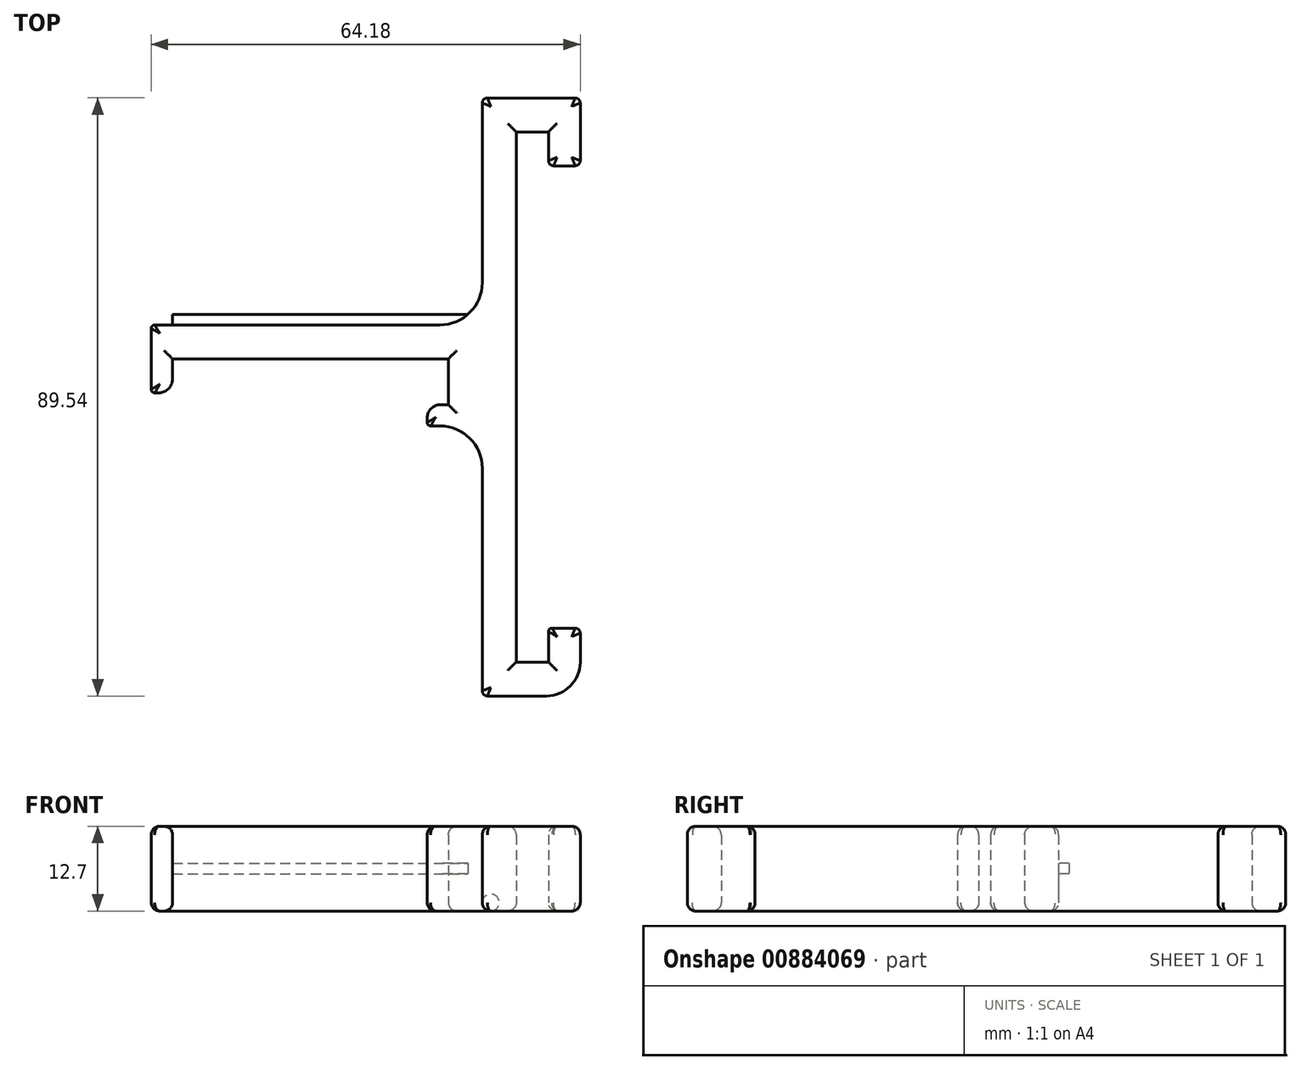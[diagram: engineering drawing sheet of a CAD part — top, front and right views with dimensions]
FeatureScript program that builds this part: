
annotation { "Feature Type Name" : "Feature", "Feature Type Description" : "" }
export const myFeature = defineFeature(function(context is Context, id is Id, definition is map)
    precondition{}
    {
        {
            var Q0;
            Q0=qCreatedBy(makeId("Top.planeOp"),FACE);
            var sketch = newSketch(context, id + "F0", { "sketchPlane" : qUnion([Q0])});
            skLineSegment(sketch, "E0", {"start": v(41.28, 0) * mm, "end": v(0, 0) * mm});
            skLineSegment(sketch, "E1", {"start": v(41.28, -6.86) * mm, "end": v(40.13, -6.86) * mm});
            skLineSegment(sketch, "E2", {"start": v(38.1, -8.89) * mm, "end": v(38.1, -9.53) * mm});
            skLineSegment(sketch, "E3", {"start": v(38.6, -10.03) * mm, "end": v(40, -10.03) * mm});
            skLineSegment(sketch, "E4", {"start": v(0, 0) * mm, "end": v(0, -3.05) * mm});
            skLineSegment(sketch, "E5.0", {"start": v(40, 5.08) * mm, "end": v(-2.67, 5.08) * mm});
            skLineSegment(sketch, "E6.0", {"start": v(-3.18, 4.57) * mm, "end": v(-3.18, -4.57) * mm});
            skLineSegment(sketch, "E7", {"start": v(-2.67, -5.08) * mm, "end": v(-2.03, -5.08) * mm});
            skLineSegment(sketch, "E8.0", {"start": v(55.92, -50.47) * mm, "end": v(47.1, -50.47) * mm});
            skLineSegment(sketch, "E9", {"start": v(46.34, -16.38) * mm, "end": v(46.34, -49.7) * mm});
            skLineSegment(sketch, "E10", {"start": v(46.34, 11.43) * mm, "end": v(46.34, 38.3) * mm});
            skLineSegment(sketch, "E11.0", {"start": v(51.42, 33.99) * mm, "end": v(51.42, -45.39) * mm});
            skLineSegment(sketch, "E12.0", {"start": v(56.25, 33.99) * mm, "end": v(56.25, 29.67) * mm});
            skLineSegment(sketch, "E13.0", {"start": v(56.25, -45.39) * mm, "end": v(51.42, -45.39) * mm});
            skLineSegment(sketch, "E14.0", {"start": v(61, -41.07) * mm, "end": v(61, -45.39) * mm});
            skLineSegment(sketch, "E15.0", {"start": v(56.25, 33.99) * mm, "end": v(51.42, 33.99) * mm});
            skLineSegment(sketch, "E16.0", {"start": v(60.24, 39.07) * mm, "end": v(47.1, 39.07) * mm});
            skLineSegment(sketch, "E17.0", {"start": v(60.24, -40.3) * mm, "end": v(56.76, -40.3) * mm});
            skLineSegment(sketch, "E18", {"start": v(56.25, -40.82) * mm, "end": v(56.25, -45.39) * mm});
            skLineSegment(sketch, "E19.0", {"start": v(60.24, 28.9) * mm, "end": v(57.01, 28.9) * mm});
            skLineSegment(sketch, "E20", {"start": v(61, 38.3) * mm, "end": v(61, 29.67) * mm});
            skLineSegment(sketch, "E21", {"start": v(41.28, 0) * mm, "end": v(41.28, -6.86) * mm});
            skPoint(sketch, "E22.visualSharp", {"position": v(61, -50.47) * mm});
            skArc(sketch, "E22.filletArc", {"start": v(55.92, -50.47) * mm, "mid": v(59.51, -48.98) * mm, "end": v(61, -45.39) * mm});
            skArc(sketch, "E23.filletArc", {"start": v(46.34, -49.7) * mm, "mid": v(46.57, -50.25) * mm, "end": v(47.1, -50.47) * mm});
            skPoint(sketch, "E24.visualSharp", {"position": v(61, -40.3) * mm});
            skArc(sketch, "E24.filletArc", {"start": v(61, -41.07) * mm, "mid": v(60.77, -40.53) * mm, "end": v(60.24, -40.3) * mm});
            skPoint(sketch, "E25.visualSharp", {"position": v(56.25, -40.3) * mm});
            skArc(sketch, "E25.filletArc", {"start": v(56.76, -40.3) * mm, "mid": v(56.4, -40.46) * mm, "end": v(56.25, -40.82) * mm});
            skPoint(sketch, "E26.visualSharp", {"position": v(56.25, 28.9) * mm});
            skArc(sketch, "E26.filletArc", {"start": v(56.25, 29.67) * mm, "mid": v(56.47, 29.13) * mm, "end": v(57.01, 28.9) * mm});
            skPoint(sketch, "E27.visualSharp", {"position": v(61, 28.9) * mm});
            skArc(sketch, "E27.filletArc", {"start": v(60.24, 28.9) * mm, "mid": v(60.77, 29.13) * mm, "end": v(61, 29.67) * mm});
            skPoint(sketch, "E28.visualSharp", {"position": v(61, 39.07) * mm});
            skArc(sketch, "E28.filletArc", {"start": v(61, 38.3) * mm, "mid": v(60.77, 38.84) * mm, "end": v(60.24, 39.07) * mm});
            skPoint(sketch, "E29.visualSharp", {"position": v(46.34, 39.07) * mm});
            skArc(sketch, "E29.filletArc", {"start": v(47.1, 39.07) * mm, "mid": v(46.57, 38.84) * mm, "end": v(46.34, 38.3) * mm});
            skPoint(sketch, "E30.visualSharp", {"position": v(46.34, 5.08) * mm});
            skArc(sketch, "E30.filletArc", {"start": v(40, 5.08) * mm, "mid": v(44.48, 6.94) * mm, "end": v(46.34, 11.43) * mm});
            skPoint(sketch, "E31.visualSharp", {"position": v(46.34, -10.03) * mm});
            skArc(sketch, "E31.filletArc", {"start": v(46.34, -16.38) * mm, "mid": v(44.48, -11.9) * mm, "end": v(40, -10.03) * mm});
            skPoint(sketch, "E32.visualSharp", {"position": v(-3.18, 5.08) * mm});
            skArc(sketch, "E32.filletArc", {"start": v(-2.67, 5.08) * mm, "mid": v(-3.03, 4.93) * mm, "end": v(-3.18, 4.57) * mm});
            skPoint(sketch, "E33.visualSharp", {"position": v(-3.18, -5.08) * mm});
            skArc(sketch, "E33.filletArc", {"start": v(-3.18, -4.57) * mm, "mid": v(-3.03, -4.93) * mm, "end": v(-2.67, -5.08) * mm});
            skPoint(sketch, "E34.visualSharp", {"position": v(38.1, -10.03) * mm});
            skArc(sketch, "E34.filletArc", {"start": v(38.1, -9.53) * mm, "mid": v(38.25, -9.88) * mm, "end": v(38.6, -10.03) * mm});
            skPoint(sketch, "E35.visualSharp", {"position": v(0, -5.08) * mm});
            skArc(sketch, "E35.filletArc", {"start": v(-2.03, -5.08) * mm, "mid": v(-0.6, -4.48) * mm, "end": v(0, -3.05) * mm});
            skPoint(sketch, "E36.visualSharp", {"position": v(38.1, -6.86) * mm});
            skArc(sketch, "E36.filletArc", {"start": v(40.13, -6.86) * mm, "mid": v(38.7, -7.45) * mm, "end": v(38.1, -8.89) * mm});
            skSolve(sketch);
        }
        {
            var Q0;
            Q0=qSketchRegion(id+"F0",true);
            extrude(context, id + "F1", {"entities" : qUnion([Q0]), "depth" : 12.7 * mm, "offsetDistance" : 25.4 * mm});
        }
        {
            var Q0;
            Q0=makeQuery(id+"F1.opExtrude","SWEPT_FACE",FACE,{"disambiguationData":[OSD([sQuery(id+"F0.wireOp",EDGE,"E5.0")])]});
            cPlane(context, id + "F2", {"entities" : qUnion([Q0]), "cplaneType" : CPlaneType.OFFSET, "offset" : 0 * mm, "width" : 152.4 * mm, "height" : 152.4 * mm});
        }
        {
            var Q0;
            Q0=qCreatedBy(id+"F2.planeOp",FACE);
            var sketch = newSketch(context, id + "F3", { "sketchPlane" : qUnion([Q0])});
            skLineSegment(sketch, "E37", {"start": v(0, 19.25) * mm, "end": v(0, 0) * mm});
            skLineSegment(sketch, "E38", {"start": v(9.05, 0) * mm, "end": v(-27.4, 0) * mm});
            skLineSegment(sketch, "E39.0", {"start": v(1.85, 7.14) * mm, "end": v(-46.34, 7.14) * mm});
            skLineSegment(sketch, "E40.0", {"start": v(-46.34, -6.35) * mm, "end": v(9.02, -6.35) * mm});
            skLineSegment(sketch, "E40.1", {"start": v(-46.34, 7.14) * mm, "end": v(-46.34, 5.56) * mm});
            skLineSegment(sketch, "E40.2", {"start": v(9.02, 19.05) * mm, "end": v(-46.34, 19.05) * mm});
            skLineSegment(sketch, "E41.0", {"start": v(1.75, 5.56) * mm, "end": v(-46.34, 5.56) * mm});
            skLineSegment(sketch, "E42", {"start": v(1.75, 5.56) * mm, "end": v(1.85, 7.14) * mm});
            skSolve(sketch);
        }
        {
            var Q0;
            {var subQ5=sQuery(id+"F3.wireOp",EDGE,"E40.1");Q0=makeQuery(id+"F3.imprint","IMPRINT",FACE,{"disambiguationData":[TD([[makeQuery(id+"F3.imprint","IMPRINT",EDGE,{"derivedFrom":subQ5}),1.0]])]});}
            extrude(context, id + "F4", {"entities" : qUnion([Q0]), "operationType" : NewBodyOperationType.ADD, "depth" : 1.59 * mm, "offsetDistance" : 25.4 * mm});
        }
        {
            var Q0;
            Q0=makeQuery(id+"F1.opExtrude","CAP_FACE",FACE,{"disambiguationData":[OSD([sQuery(id+"F0.wireOp",EDGE,"E0"),sQuery(id+"F0.wireOp",EDGE,"E1"),sQuery(id+"F0.wireOp",EDGE,"E2"),sQuery(id+"F0.wireOp",EDGE,"E3"),sQuery(id+"F0.wireOp",EDGE,"E4"),sQuery(id+"F0.wireOp",EDGE,"E5.0"),sQuery(id+"F0.wireOp",EDGE,"E6.0"),sQuery(id+"F0.wireOp",EDGE,"E7"),sQuery(id+"F0.wireOp",EDGE,"E8.0"),sQuery(id+"F0.wireOp",EDGE,"E9"),sQuery(id+"F0.wireOp",EDGE,"E10"),sQuery(id+"F0.wireOp",EDGE,"E11.0"),sQuery(id+"F0.wireOp",EDGE,"E12.0"),sQuery(id+"F0.wireOp",EDGE,"E13.0"),sQuery(id+"F0.wireOp",EDGE,"E14.0"),sQuery(id+"F0.wireOp",EDGE,"E15.0"),sQuery(id+"F0.wireOp",EDGE,"E16.0"),sQuery(id+"F0.wireOp",EDGE,"E17.0"),sQuery(id+"F0.wireOp",EDGE,"E18"),sQuery(id+"F0.wireOp",EDGE,"E19.0"),sQuery(id+"F0.wireOp",EDGE,"E20"),sQuery(id+"F0.wireOp",EDGE,"E21"),sQuery(id+"F0.wireOp",EDGE,"E22.filletArc"),sQuery(id+"F0.wireOp",EDGE,"E23.filletArc"),sQuery(id+"F0.wireOp",EDGE,"E24.filletArc"),sQuery(id+"F0.wireOp",EDGE,"E25.filletArc"),sQuery(id+"F0.wireOp",EDGE,"E26.filletArc"),sQuery(id+"F0.wireOp",EDGE,"E27.filletArc"),sQuery(id+"F0.wireOp",EDGE,"E28.filletArc"),sQuery(id+"F0.wireOp",EDGE,"E29.filletArc"),sQuery(id+"F0.wireOp",EDGE,"E30.filletArc"),sQuery(id+"F0.wireOp",EDGE,"E31.filletArc"),sQuery(id+"F0.wireOp",EDGE,"E32.filletArc"),sQuery(id+"F0.wireOp",EDGE,"E33.filletArc"),sQuery(id+"F0.wireOp",EDGE,"E34.filletArc"),sQuery(id+"F0.wireOp",EDGE,"E35.filletArc"),sQuery(id+"F0.wireOp",EDGE,"E36.filletArc")])],"isStart":false});
            fillet(context, id + "F5", {"entities" : qUnion([Q0]), "radius" : 1.27 * mm, "tangentPropagation" : true, "allowEdgeOverflow" : false});
        }
        {
            var Q0;
            Q0=makeQuery(id+"F1.opExtrude","CAP_FACE",FACE,{"disambiguationData":[OSD([sQuery(id+"F0.wireOp",EDGE,"E0"),sQuery(id+"F0.wireOp",EDGE,"E1"),sQuery(id+"F0.wireOp",EDGE,"E2"),sQuery(id+"F0.wireOp",EDGE,"E3"),sQuery(id+"F0.wireOp",EDGE,"E4"),sQuery(id+"F0.wireOp",EDGE,"E5.0"),sQuery(id+"F0.wireOp",EDGE,"E6.0"),sQuery(id+"F0.wireOp",EDGE,"E7"),sQuery(id+"F0.wireOp",EDGE,"E8.0"),sQuery(id+"F0.wireOp",EDGE,"E9"),sQuery(id+"F0.wireOp",EDGE,"E10"),sQuery(id+"F0.wireOp",EDGE,"E11.0"),sQuery(id+"F0.wireOp",EDGE,"E12.0"),sQuery(id+"F0.wireOp",EDGE,"E13.0"),sQuery(id+"F0.wireOp",EDGE,"E14.0"),sQuery(id+"F0.wireOp",EDGE,"E15.0"),sQuery(id+"F0.wireOp",EDGE,"E16.0"),sQuery(id+"F0.wireOp",EDGE,"E17.0"),sQuery(id+"F0.wireOp",EDGE,"E18"),sQuery(id+"F0.wireOp",EDGE,"E19.0"),sQuery(id+"F0.wireOp",EDGE,"E20"),sQuery(id+"F0.wireOp",EDGE,"E21"),sQuery(id+"F0.wireOp",EDGE,"E22.filletArc"),sQuery(id+"F0.wireOp",EDGE,"E23.filletArc"),sQuery(id+"F0.wireOp",EDGE,"E24.filletArc"),sQuery(id+"F0.wireOp",EDGE,"E25.filletArc"),sQuery(id+"F0.wireOp",EDGE,"E26.filletArc"),sQuery(id+"F0.wireOp",EDGE,"E27.filletArc"),sQuery(id+"F0.wireOp",EDGE,"E28.filletArc"),sQuery(id+"F0.wireOp",EDGE,"E29.filletArc"),sQuery(id+"F0.wireOp",EDGE,"E30.filletArc"),sQuery(id+"F0.wireOp",EDGE,"E31.filletArc"),sQuery(id+"F0.wireOp",EDGE,"E32.filletArc"),sQuery(id+"F0.wireOp",EDGE,"E33.filletArc"),sQuery(id+"F0.wireOp",EDGE,"E34.filletArc"),sQuery(id+"F0.wireOp",EDGE,"E35.filletArc"),sQuery(id+"F0.wireOp",EDGE,"E36.filletArc")])],"isStart":true});
            fillet(context, id + "F6", {"entities" : qUnion([Q0]), "radius" : 1.27 * mm, "tangentPropagation" : true, "allowEdgeOverflow" : false});
        }
    });
